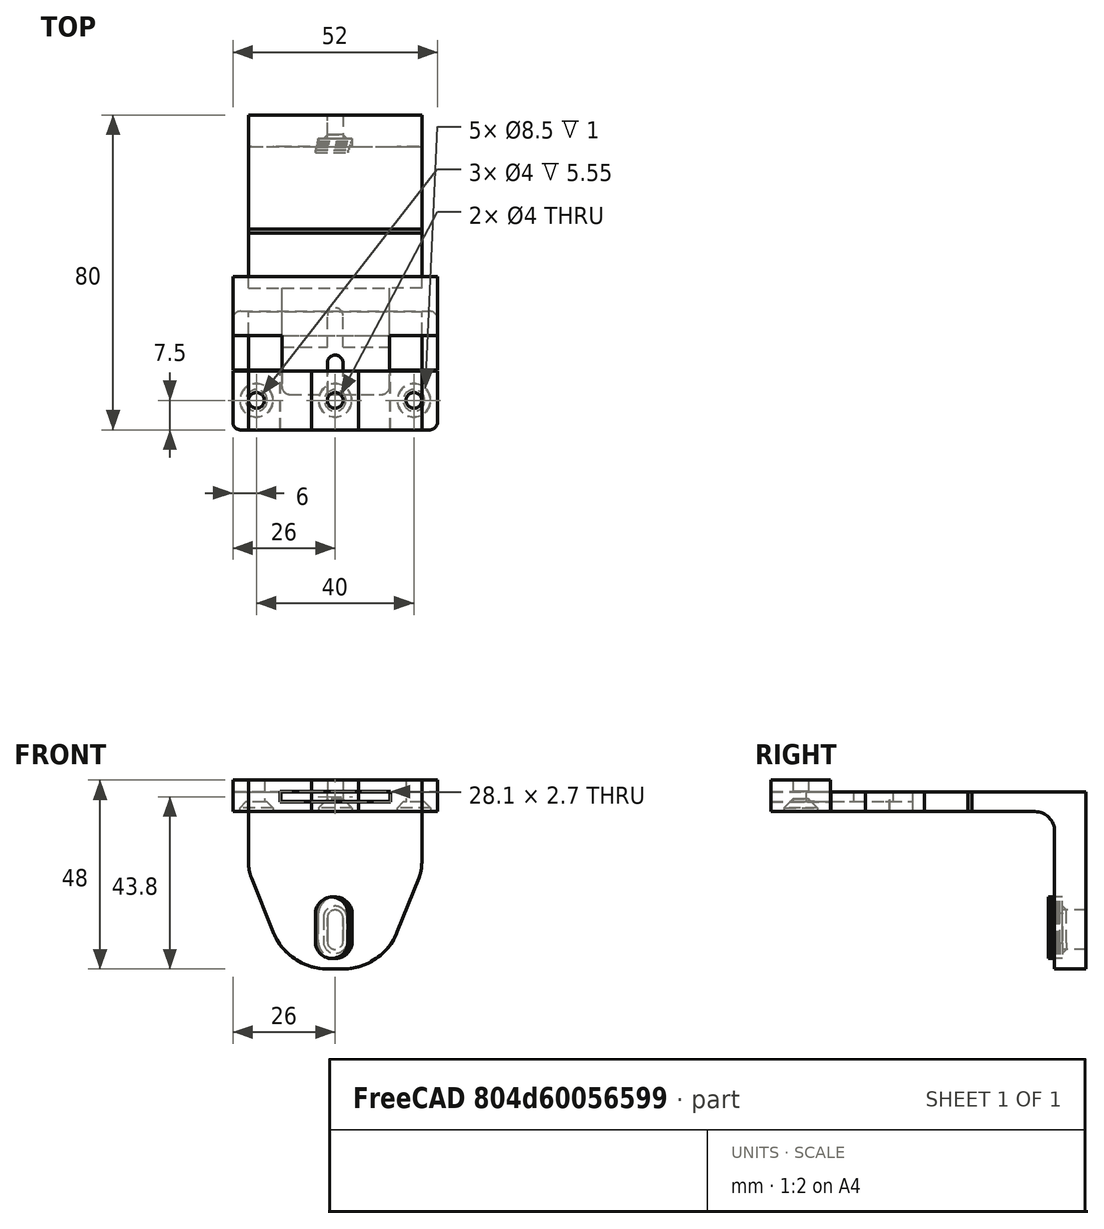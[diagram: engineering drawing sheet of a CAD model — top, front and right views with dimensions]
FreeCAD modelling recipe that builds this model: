
FCSTD DOCUMENT  (FreeCAD 0.19R24267 +99 (Git))
Label: piezas_banio_techo
License: CreativeCommons Attribution-ShareAlike
LicenseURL: http://creativecommons.org/licenses/by-sa/4.0/
objects: Part::Box×45, Part::MultiFuse×31, Part::Cut×30, Part::Cylinder×25, Part::Fillet×9, Part::Chamfer×7, Part::Feature×7, Part::FeaturePython×7, App::FeaturePython×4, App::AnnotationLabel×4, Sketcher::SketchObject×2, Part::Extrusion×2, Mesh::Feature×2, App::DocumentObjectGroup×1
note: 165 computed .brp shape members not serialized (recipe doc carries the construction recipe); baked Part::Feature solids carry a one-line shape summary decoded from their .brp

FEATURE [Part::Box] Box  label="Cube"
  AttacherType = Attacher::AttachEngine3D
  Height = 5
  Length = 44
  Width = 30
FEATURE [Part::Box] Box001  label="Cube001"
  AttacherType = Attacher::AttachEngine3D
  Height = 8
  Length = 44
  Width = 15
FEATURE [Part::MultiFuse] Fusion
  Shapes = -> [Box,Box001]
FEATURE [Part::Cylinder] Cylinder
  Angle = 360
  AttacherType = Attacher::AttachEngine3D
  Height = 10
  Placement = pos=(22,7.5,0) rot=(0,0,1;0rad)
  Radius = 2
FEATURE [Part::Cylinder] Cylinder001
  Angle = 360
  AttacherType = Attacher::AttachEngine3D
  Height = 10
  Placement = pos=(22,7.5,7) rot=(0,0,1;0rad)
  Radius = 4.25
FEATURE [Part::MultiFuse] Fusion001
  Shapes = -> [Cylinder,Cylinder001]
FEATURE [Part::Cut] Cut
  Base = -> Fusion
  Tool = -> Fusion001
FEATURE [Part::Chamfer] Chamfer  label="pieza_exterior_x_4_1"
  Base = -> Cut
  Edges = 1 edges r=2.2: [Edge31]
FEATURE [Part::Box] Box002  label="Cube002"
  AttacherType = Attacher::AttachEngine3D
  Height = 5
  Length = 44
  Placement = pos=(0,50,0) rot=(0,0,1;0rad)
  Width = 30
FEATURE [Part::Box] Box003  label="Cube003"
  AttacherType = Attacher::AttachEngine3D
  Height = 15
  Length = 44
  Placement = pos=(0,72,-15) rot=(0,0,1;0rad)
  Width = 8
FEATURE [Part::MultiFuse] Fusion002
  Shapes = -> [Box002,Box003]
FEATURE [Part::Fillet] Fillet
  Base = -> Fusion002
  Edges = 1 edges r=5: [Edge13]
FEATURE [Part::Box] Box004  label="Cube004"
  AttacherType = Attacher::AttachEngine3D
  Height = 45
  Length = 24
  Placement = pos=(10,72,-40) rot=(0,0,1;0rad)
  Width = 8
FEATURE [Part::MultiFuse] Fusion003
  Shapes = -> [Fillet,Box004]
FEATURE [Sketcher::SketchObject] Sketch
  ExternalGeometry = -> [Fusion003]
  FullyConstrained = false
  MapMode = 5
  Placement = pos=(0,80,0) rot=(0,0.707107,0.707107;3.14159rad)
  Support = -> [Fusion003]
  sketch-geometry (6):
    g0: LineSegment StartX=-44 StartY=-15 StartZ=0 EndX=-34 EndY=-40 EndZ=0
    g1: LineSegment StartX=-34 StartY=-40 StartZ=0 EndX=-34 EndY=-15 EndZ=0
    g2: LineSegment StartX=-34 StartY=-15 StartZ=0 EndX=-44 EndY=-15 EndZ=0
    g3: LineSegment StartX=-10 StartY=-15 StartZ=0 EndX=0 EndY=-15 EndZ=0
    g4: LineSegment StartX=0 StartY=-15 StartZ=0 EndX=-10 EndY=-40 EndZ=0
    g5: LineSegment StartX=-10 StartY=-40 StartZ=0 EndX=-10 EndY=-15 EndZ=0
  constraints (12):
    c: Coincident(g0,g1)
    c: Coincident(g1,g2)
    c: Coincident(g0,g2)
    c: Coincident(g0,g-3)
    c: Coincident(g1,g-3)
    c: Coincident(g0,g-4)
    c: Coincident(g3,g4)
    c: Coincident(g4,g5)
    c: Coincident(g3,g5)
    c: Coincident(g3,g-5)
    c: Coincident(g3,g-5)
    c: Coincident(g4,g-4)
FEATURE [Part::Extrusion] Extrude
  Base = -> Sketch
  Dir = (0,1,-2e-16)
  DirMode = 2
  FaceMakerClass = Part::FaceMakerBullseye
  LengthFwd = -8
  LengthRev = 0
  Solid = true
  Symmetric = false
FEATURE [Part::MultiFuse] Fusion004
  Shapes = -> [Fusion003,Extrude]
FEATURE [Part::Fillet] Fillet001
  Base = -> Fusion004
  Edges = 2 edges r=15: [Edge12,Edge14]
FEATURE [Part::Fillet] Fillet002
  Base = -> Fillet001
  Edges = 2 edges r=10: [Edge26,Edge39]
FEATURE [Part::Cylinder] Cylinder002
  Angle = 360
  AttacherType = Attacher::AttachEngine3D
  Height = 10
  Placement = pos=(22,89,-33) rot=(1,0,0;1.5708rad)
  Radius = 4.25
FEATURE [Part::Cylinder] Cylinder003
  Angle = 360
  AttacherType = Attacher::AttachEngine3D
  Height = 10
  Placement = pos=(22,80,-33) rot=(1,0,0;1.5708rad)
  Radius = 2
FEATURE [Part::MultiFuse] Fusion005
  Shapes = -> [Cylinder002,Cylinder003]
FEATURE [Part::Cut] Cut001
  Base = -> Fillet002
  Tool = -> Fusion005
FEATURE [Part::Chamfer] Chamfer001  label="pieza_interior_x4_1"
  Base = -> Cut001
  Edges = 1 edges r=2.2: [Edge50]
FEATURE [Part::Cylinder] Cylinder004
  Angle = 360
  AttacherType = Attacher::AttachEngine3D
  Height = 10
  Placement = pos=(22,80,-33) rot=(1,0,0;1.5708rad)
  Radius = 2
FEATURE [Part::Cylinder] Cylinder005
  Angle = 360
  AttacherType = Attacher::AttachEngine3D
  Height = 10
  Placement = pos=(22,89,-33) rot=(1,0,0;1.5708rad)
  Radius = 4.25
FEATURE [Part::MultiFuse] Fusion006
  Placement = pos=(0,152,-66) rot=(1,0,0;3.14159rad)
  Shapes = -> [Cylinder005,Cylinder004]
FEATURE [Part::Cylinder] Cylinder006
  Angle = 360
  AttacherType = Attacher::AttachEngine3D
  Height = 10
  Placement = pos=(22,80,-33) rot=(1,0,0;1.5708rad)
  Radius = 4.25
FEATURE [Part::MultiFuse] Fusion007
  Shapes = -> [Chamfer001,Cylinder006]
FEATURE [Part::Cut] Cut002
  Base = -> Fusion007
  Tool = -> Fusion006
FEATURE [Part::Chamfer] Chamfer002  label="pieza_interior_x4"
  Base = -> Cut002
  Edges = 1 edges r=2.2: [Edge55]
FEATURE [Part::Cylinder] Cylinder007
  Angle = 360
  AttacherType = Attacher::AttachEngine3D
  Height = 10
  Placement = pos=(22,7.5,7) rot=(0,0,1;0rad)
  Radius = 4.25
FEATURE [Part::Cylinder] Cylinder008
  Angle = 360
  AttacherType = Attacher::AttachEngine3D
  Height = 10
  Placement = pos=(22,7.5,0) rot=(0,0,1;0rad)
  Radius = 2
FEATURE [Part::MultiFuse] Fusion008
  Placement = pos=(0,15,8) rot=(1,0,0;3.14159rad)
  Shapes = -> [Cylinder008,Cylinder007]
FEATURE [Part::Cylinder] Cylinder009
  Angle = 360
  AttacherType = Attacher::AttachEngine3D
  Height = 8
  Placement = pos=(22,7.5,0) rot=(0,0,1;0rad)
  Radius = 4.25
FEATURE [Part::MultiFuse] Fusion009
  Shapes = -> [Chamfer,Cylinder009]
FEATURE [Part::Cut] Cut003
  Base = -> Fusion009
  Tool = -> Fusion008
FEATURE [Part::Chamfer] Chamfer003  label="pieza_exterior_x_4"
  Base = -> Cut003
  Edges = 1 edges r=2.2: [Edge7]
FEATURE [Part::Cylinder] Cylinder010
  Angle = 360
  AttacherType = Attacher::AttachEngine3D
  Height = 10
  Placement = pos=(22,80,-33) rot=(1,0,0;1.5708rad)
  Radius = 4.25
FEATURE [Part::Cylinder] Cylinder011
  Angle = 360
  AttacherType = Attacher::AttachEngine3D
  Height = 10
  Placement = pos=(22,80,-33) rot=(1,0,0;1.5708rad)
  Radius = 2
FEATURE [Part::Box] Box005  label="Cube005"
  AttacherType = Attacher::AttachEngine3D
  Height = 5
  Length = 44
  Placement = pos=(0,50,0) rot=(0,0,1;0rad)
  Width = 30
FEATURE [Part::Cylinder] Cylinder012
  Angle = 360
  AttacherType = Attacher::AttachEngine3D
  Height = 10
  Placement = pos=(22,89,-33) rot=(1,0,0;1.5708rad)
  Radius = 4.25
FEATURE [Part::Box] Box006  label="Cube006"
  AttacherType = Attacher::AttachEngine3D
  Height = 15
  Length = 44
  Placement = pos=(0,72,-15) rot=(0,0,1;0rad)
  Width = 8
FEATURE [Part::Box] Box007  label="Cube007"
  AttacherType = Attacher::AttachEngine3D
  Height = 45
  Length = 24
  Placement = pos=(10,72,-40) rot=(0,0,1;0rad)
  Width = 8
FEATURE [Part::Cylinder] Cylinder013
  Angle = 360
  AttacherType = Attacher::AttachEngine3D
  Height = 10
  Placement = pos=(22,80,-33) rot=(1,0,0;1.5708rad)
  Radius = 2
FEATURE [Part::Cylinder] Cylinder014
  Angle = 360
  AttacherType = Attacher::AttachEngine3D
  Height = 10
  Placement = pos=(22,89,-33) rot=(1,0,0;1.5708rad)
  Radius = 4.25
FEATURE [Part::MultiFuse] Fusion010
  Shapes = -> [Cylinder012,Cylinder011]
FEATURE [Part::MultiFuse] Fusion013
  Placement = pos=(0,152,-66) rot=(1,0,0;3.14159rad)
  Shapes = -> [Cylinder014,Cylinder013]
FEATURE [Part::MultiFuse] Fusion014
  Shapes = -> [Box005,Box006]
FEATURE [Part::Fillet] Fillet003
  Base = -> Fusion014
  Edges = 1 edges r=5: [Edge13]
FEATURE [Part::MultiFuse] Fusion012
  Shapes = -> [Fillet003,Box007]
FEATURE [Sketcher::SketchObject] Sketch001
  ExternalGeometry = -> [Fusion012]
  FullyConstrained = false
  MapMode = 5
  Placement = pos=(0,80,0) rot=(0,0.707107,0.707107;3.14159rad)
  Support = -> [Fusion012]
  sketch-geometry (6):
    g0: LineSegment StartX=-44 StartY=-15 StartZ=0 EndX=-34 EndY=-40 EndZ=0
    g1: LineSegment StartX=-34 StartY=-40 StartZ=0 EndX=-34 EndY=-15 EndZ=0
    g2: LineSegment StartX=-34 StartY=-15 StartZ=0 EndX=-44 EndY=-15 EndZ=0
    g3: LineSegment StartX=-10 StartY=-15 StartZ=0 EndX=0 EndY=-15 EndZ=0
    g4: LineSegment StartX=0 StartY=-15 StartZ=0 EndX=-10 EndY=-40 EndZ=0
    g5: LineSegment StartX=-10 StartY=-40 StartZ=0 EndX=-10 EndY=-15 EndZ=0
  constraints (12):
    c: Coincident(g0,g1)
    c: Coincident(g1,g2)
    c: Coincident(g0,g2)
    c: Coincident(g0,g-3)
    c: Coincident(g1,g-3)
    c: Coincident(g0,g-4)
    c: Coincident(g3,g4)
    c: Coincident(g4,g5)
    c: Coincident(g3,g5)
    c: Coincident(g3,g-5)
    c: Coincident(g3,g-5)
    c: Coincident(g4,g-4)
FEATURE [Part::Extrusion] Extrude001
  Base = -> Sketch001
  Dir = (0,1,-2e-16)
  DirMode = 2
  FaceMakerClass = Part::FaceMakerBullseye
  LengthFwd = -8
  LengthRev = 0
  Solid = true
  Symmetric = false
FEATURE [Part::MultiFuse] Fusion015
  Shapes = -> [Fusion012,Extrude001]
FEATURE [Part::Fillet] Fillet005
  Base = -> Fusion015
  Edges = 2 edges r=15: [Edge12,Edge14]
FEATURE [Part::Fillet] Fillet004
  Base = -> Fillet005
  Edges = 2 edges r=10: [Edge26,Edge39]
FEATURE [Part::Cut] Cut004
  Base = -> Fillet004
  Tool = -> Fusion010
FEATURE [Part::Chamfer] Chamfer004  label="pieza_interior_x4_002"
  Base = -> Cut004
  Edges = 1 edges r=2.2: [Edge50]
FEATURE [Part::MultiFuse] Fusion011
  Shapes = -> [Chamfer004,Cylinder010]
FEATURE [Part::Cut] Cut005
  Base = -> Fusion011
  Tool = -> Fusion013
FEATURE [Part::Chamfer] Chamfer005  label="pieza_interior_x005"
  Base = -> Cut005
  Edges = 1 edges r=2.2: [Edge55]
FEATURE [Part::Cylinder] Cylinder015
  Angle = 360
  AttacherType = Attacher::AttachEngine3D
  Height = 10
  Placement = pos=(22,80,-27) rot=(1,0,0;1.5708rad)
  Radius = 2
FEATURE [Part::Box] Box008  label="Cube008"
  AttacherType = Attacher::AttachEngine3D
  Height = 6
  Length = 4
  Placement = pos=(20,69,-33) rot=(0,0,1;0rad)
  Width = 16
FEATURE [Part::MultiFuse] Fusion016
  Shapes = -> [Box008,Cylinder015]
FEATURE [Part::Cylinder] Cylinder016
  Angle = 360
  AttacherType = Attacher::AttachEngine3D
  Height = 10
  Placement = pos=(22,73,-33) rot=(1,0,0;1.5708rad)
  Radius = 4.3
FEATURE [Part::Cylinder] Cylinder017
  Angle = 360
  AttacherType = Attacher::AttachEngine3D
  Height = 10
  Placement = pos=(22,73,-26) rot=(1,0,0;1.5708rad)
  Radius = 4.3
FEATURE [Part::Box] Box009  label="Cube009"
  AttacherType = Attacher::AttachEngine3D
  Height = 7.6
  Length = 8.6
  Placement = pos=(17.7,59,-33.3) rot=(0,0,1;0rad)
  Width = 14
FEATURE [Part::MultiFuse] Fusion017  label="corta_grande"
  Placement = pos=(0,1,0) rot=(0,0,1;0rad)
  Shapes = -> [Cylinder016,Box009,Cylinder017]
FEATURE [Part::Cylinder] Cylinder018
  Angle = 360
  AttacherType = Attacher::AttachEngine3D
  Height = 10
  Placement = pos=(22,80,-33) rot=(1,0,0;1.5708rad)
  Radius = 2
FEATURE [Part::Cylinder] Cylinder019
  Angle = 360
  AttacherType = Attacher::AttachEngine3D
  Height = 10
  Placement = pos=(22,89,-33) rot=(1,0,0;1.5708rad)
  Radius = 4.25
FEATURE [Part::MultiFuse] Fusion018
  Shapes = -> [Cylinder019,Cylinder018]
FEATURE [Part::MultiFuse] Fusion019  label="corta_chico"
  Placement = pos=(0,2,0) rot=(0,0,1;0rad)
  Shapes = -> [Fusion016,Fusion018]
FEATURE [Part::Box] Box010  label="Cube010"
  AttacherType = Attacher::AttachEngine3D
  Height = 10
  Length = 15
  Placement = pos=(14,72,-38) rot=(0,0,1;0rad)
  Width = 8
FEATURE [Part::MultiFuse] Fusion020
  Shapes = -> [Chamfer005,Box010]
FEATURE [Part::Cut] Cut006
  Base = -> Fusion020
  Tool = -> Fusion019
FEATURE [Part::Box] Box011  label="Cube011"
  AttacherType = Attacher::AttachEngine3D
  Height = 7.6
  Length = 8.6
  Placement = pos=(17.7,59,-33.3) rot=(0,0,1;0rad)
  Width = 14
FEATURE [Part::Cylinder] Cylinder020
  Angle = 360
  AttacherType = Attacher::AttachEngine3D
  Height = 10
  Placement = pos=(22,73,-33) rot=(1,0,0;1.5708rad)
  Radius = 4.3
FEATURE [Part::Cylinder] Cylinder021
  Angle = 360
  AttacherType = Attacher::AttachEngine3D
  Height = 10
  Placement = pos=(22,73,-26) rot=(1,0,0;1.5708rad)
  Radius = 4.3
FEATURE [Part::MultiFuse] Fusion021  label="corta_grande001"
  Placement = pos=(0,1,0) rot=(0,0,1;0rad)
  Shapes = -> [Cylinder020,Box011,Cylinder021]
FEATURE [Part::Cut] Cut007
  Base = -> Cut006
  Tool = -> Fusion017
FEATURE [Part::Feature] Cut007001  label="Cut008"
  shape: bbox 44 x 30 x 45 mm, 28 faces (baked)
FEATURE [Part::Chamfer] Chamfer006  label="pieza_exterior_x4_movil"
  Base = -> Cut007001
  Edges = 8 edges r=1: [Edge59,Edge60,Edge61,Edge62,Edge63,Edge64,Edge65,Edge66]
FEATURE [Part::Box] Box012  label="Cube012"
  AttacherType = Attacher::AttachEngine3D
  Height = 20
  Length = 20
  Placement = pos=(10,53.4,-39) rot=(0,0,1;0rad)
  Width = 20
FEATURE [Part::Cut] Cut007002  label="tapita"
  Base = -> Fusion021
  Tool = -> Box012
FEATURE [Part::Feature] Cut007002001  label="Scale_100"
  shape: bbox 8.6 x 0.6 x 15.6 mm, 10 faces (baked)
FEATURE [Part::FeaturePython] Scale  label="Scale_096"  # Draft clone (typed FeaturePython)
  Fuse = false
  Objects = -> [Cut007002001]
  Scale = (0.96,0.96,1)
FEATURE [Part::FeaturePython] Scale001  label="Scale_097"  # Draft clone (typed FeaturePython)
  Fuse = false
  Objects = -> [Cut007002001]
  Scale = (0.97,0.97,1)
FEATURE [Part::FeaturePython] Scale002  label="Scale_098"  # Draft clone (typed FeaturePython)
  Fuse = false
  Objects = -> [Cut007002001]
  Scale = (0.98,0.98,1)
FEATURE [Part::FeaturePython] Scale003  label="Scale_099"  # Draft clone (typed FeaturePython)
  Fuse = false
  Objects = -> [Cut007002001]
  Scale = (0.99,0.99,1)
FEATURE [Part::Box] Box013  label="Cube013"
  AttacherType = Attacher::AttachEngine3D
  Height = 5
  Length = 44
  Width = 30
FEATURE [Part::Box] Box014  label="Cube014"
  AttacherType = Attacher::AttachEngine3D
  Height = 2.6
  Length = 44
  Width = 15
FEATURE [Part::Cut] Cut007002002
  Base = -> Box013
  Tool = -> Box014
FEATURE [Part::Box] Box015  label="Cube015"
  AttacherType = Attacher::AttachEngine3D
  Height = 10
  Length = 8.52
  Width = 15
FEATURE [Part::Box] Box016  label="Cube016"
  AttacherType = Attacher::AttachEngine3D
  Height = 10
  Length = 8.2
  Placement = pos=(35.8,0,0) rot=(0,0,1;0rad)
  Width = 15
FEATURE [Part::Cut] Cut007002003
  Base = -> Cut007002002
  Tool = -> Box015
FEATURE [Part::Cut] Cut007002004  label="exterior_part1_1"
  Base = -> Cut007002003
  Tool = -> Box016
FEATURE [Part::Cylinder] Cylinder022
  Angle = 360
  AttacherType = Attacher::AttachEngine3D
  Height = 10
  Placement = pos=(22,8,0) rot=(0,0,1;0rad)
  Radius = 2
FEATURE [Part::Box] Box017  label="Cube017"
  AttacherType = Attacher::AttachEngine3D
  Height = 10
  Length = 4
  Placement = pos=(20,-8,0) rot=(0,0,1;0rad)
  Width = 16
FEATURE [Part::MultiFuse] Fusion022
  Shapes = -> [Cylinder022,Box017]
FEATURE [Part::Cut] Cut007002005  label="exterior_part1"
  Base = -> Cut007002004
  Placement = pos=(0,21,0) rot=(0,0,1;0rad)
  Tool = -> Fusion022
FEATURE [Part::Feature] Chamfer003001  label="pieza_exterior_x_005"
  shape: bbox 44 x 30 x 8 mm, 12 faces (baked)
FEATURE [Part::Box] Box018  label="Cube018"
  AttacherType = Attacher::AttachEngine3D
  Height = 2.5
  Length = 28
  Placement = pos=(8,0,2.55) rot=(0,0,1;0rad)
  Width = 22
FEATURE [Part::Cut] Cut007002006
  Base = -> Chamfer003001
  Tool = -> Box018
FEATURE [Part::Box] Box019  label="Cube019"
  AttacherType = Attacher::AttachEngine3D
  Height = 10
  Length = 44
  Placement = pos=(0,15,0) rot=(0,0,1;0rad)
  Width = 20
FEATURE [Part::Cut] Cut007002007  label="exterior_part21"
  Base = -> Cut007002006
  Tool = -> Box019
FEATURE [Part::Box] Box020  label="Cube020"
  AttacherType = Attacher::AttachEngine3D
  Height = 2.7
  Length = 28.1
  Placement = pos=(7.95,-2,2.45) rot=(0,0,1;0rad)
  Width = 20
FEATURE [Part::Cut] Cut007002008  label="exterior_part2"
  Base = -> Cut007002007
  Tool = -> Box020
FEATURE [Part::Box] Box021  label="Cube021"
  AttacherType = Attacher::AttachEngine3D
  Height = 2.5
  Length = 28
  Placement = pos=(8,0,2.55) rot=(0,0,1;0rad)
  Width = 22
FEATURE [Part::Box] Box022  label="Cube022"
  AttacherType = Attacher::AttachEngine3D
  Height = 10
  Length = 44
  Placement = pos=(0,15,0) rot=(0,0,1;0rad)
  Width = 20
FEATURE [Part::Box] Box023  label="Cube023"
  AttacherType = Attacher::AttachEngine3D
  Height = 2.7
  Length = 28.1
  Placement = pos=(7.95,-2,2.45) rot=(0,0,1;0rad)
  Width = 20
FEATURE [Part::Feature] Chamfer003002  label="pieza_exterior_x_006"
  shape: bbox 44 x 30 x 8 mm, 12 faces (baked)
FEATURE [Part::Cut] Cut007002009
  Base = -> Chamfer003002
  Tool = -> Box021
FEATURE [Part::Cut] Cut007002010  label="exterior_part022"
  Base = -> Cut007002009
  Tool = -> Box022
FEATURE [Part::Cut] Cut007002011  label="nuevo_exterior_atornillada"
  Base = -> Cut007002010
  Tool = -> Box023
FEATURE [Part::Box] Box024  label="Cube024"
  AttacherType = Attacher::AttachEngine3D
  Height = 8
  Length = 10
  Placement = pos=(-4,0,0) rot=(0,0,1;0rad)
  Width = 15
FEATURE [Part::Box] Box025  label="Cube025"
  AttacherType = Attacher::AttachEngine3D
  Height = 8
  Length = 10
  Placement = pos=(38,0,0) rot=(0,0,1;0rad)
  Width = 15
FEATURE [Part::MultiFuse] Fusion023  label="exterior_parte1_V2_0001"
  Refine = true
  Shapes = -> [Cut007002011,Box024,Box025]
FEATURE [Part::Box] Box026  label="Cube026"
  AttacherType = Attacher::AttachEngine3D
  Height = 5
  Length = 44
  Width = 30
FEATURE [Part::Box] Box027  label="Cube027"
  AttacherType = Attacher::AttachEngine3D
  Height = 2.6
  Length = 44
  Width = 15
FEATURE [Part::Box] Box028  label="Cube028"
  AttacherType = Attacher::AttachEngine3D
  Height = 10
  Length = 8.52
  Width = 15
FEATURE [Part::Box] Box029  label="Cube029"
  AttacherType = Attacher::AttachEngine3D
  Height = 10
  Length = 8.2
  Placement = pos=(35.8,0,0) rot=(0,0,1;0rad)
  Width = 15
FEATURE [Part::Box] Box030  label="Cube030"
  AttacherType = Attacher::AttachEngine3D
  Height = 10
  Length = 4
  Placement = pos=(20,-8,0) rot=(0,0,1;0rad)
  Width = 16
FEATURE [Part::Cut] Cut007002012
  Base = -> Box026
  Tool = -> Box027
FEATURE [Part::Cut] Cut007002013
  Base = -> Cut007002012
  Tool = -> Box028
FEATURE [Part::Cut] Cut007002014  label="exterior_part1_002"
  Base = -> Cut007002013
  Tool = -> Box029
FEATURE [Part::Cylinder] Cylinder023
  Angle = 360
  AttacherType = Attacher::AttachEngine3D
  Height = 10
  Placement = pos=(22,8,0) rot=(0,0,1;0rad)
  Radius = 2
FEATURE [Part::MultiFuse] Fusion024
  Shapes = -> [Cylinder023,Box030]
FEATURE [Part::Cut] Cut007002015  label="exterior_part023"
  Base = -> Cut007002014
  Placement = pos=(0,21,0) rot=(0,0,1;0rad)
  Tool = -> Fusion024
FEATURE [Part::Box] Box031  label="Cube031"
  AttacherType = Attacher::AttachEngine3D
  Height = 5
  Length = 10
  Placement = pos=(-4,36,0) rot=(0,0,1;0rad)
  Width = 15
FEATURE [Part::Box] Box032  label="Cube032"
  AttacherType = Attacher::AttachEngine3D
  Height = 5
  Length = 10
  Placement = pos=(38,36,0) rot=(0,0,1;0rad)
  Width = 15
FEATURE [Part::MultiFuse] Fusion025
  Refine = true
  Shapes = -> [Cut007002015,Box031,Box032]
FEATURE [Part::Box] Box033  label="Cube033"
  AttacherType = Attacher::AttachEngine3D
  Height = 2.4
  Length = 27.28
  Placement = pos=(8.5,21,2.5) rot=(0,0,1;0rad)
  Width = 15
FEATURE [Part::MultiFuse] Fusion026
  Refine = true
  Shapes = -> [Fusion025,Box033]
FEATURE [Part::Fillet] Fillet006  label="exterior_parte2_V2_base"
  Base = -> Fusion026
  Edges = 2 edges r=2: [Edge8,Edge43]
  Placement = pos=(0,-12,0.05) rot=(0,0,1;0rad)
FEATURE [Part::Feature] Fusion023001
  shape: bbox 52 x 15 x 8 mm, 14 faces (baked)
FEATURE [Part::Box] Box034  label="Cube034"
  AttacherType = Attacher::AttachEngine3D
  Height = 5.55
  Length = 15
  Placement = pos=(14,0,2.45) rot=(0,0,1;0rad)
  Width = 15
FEATURE [Part::Cylinder] Cylinder024
  Angle = 360
  AttacherType = Attacher::AttachEngine3D
  Height = 17
  Placement = pos=(22,7.5,0) rot=(0,0,1;0rad)
  Radius = 2
FEATURE [Part::Cut] Cut007002016
  Base = -> Box034
  Refine = true
  Tool = -> Cylinder024
FEATURE [Part::MultiFuse] Fusion023002
  Refine = true
  Shapes = -> [Fusion023001,Cut007002016]
FEATURE [Part::Box] Box035  label="Cube035"
  AttacherType = Attacher::AttachEngine3D
  Height = 11
  Length = 20
  Placement = pos=(-4,0,0) rot=(0,0,1;0rad)
  Width = 15
FEATURE [Part::Box] Box036  label="Cube036"
  AttacherType = Attacher::AttachEngine3D
  Height = 11
  Length = 20
  Placement = pos=(28,0,0) rot=(0,0,1;0rad)
  Width = 15
FEATURE [Part::Cut] Cut007002017
  Base = -> Fusion023002
  Refine = true
  Tool = -> Box035
FEATURE [Part::Cut] Cut007002018
  Base = -> Cut007002017
  Refine = true
  Tool = -> Box036
FEATURE [Part::Feature] Cut007002018_solid  label="Cut007002018 (Solid)"
  Placement = pos=(-20,0,0) rot=(0,0,1;0rad)
  shape: bbox 12 x 15 x 8 mm, 11 faces (baked)
FEATURE [Part::Feature] Cut007002018_solid001  label="Cut007002018 (Solid)001"
  Placement = pos=(20,0,0) rot=(0,0,1;0rad)
  shape: bbox 12 x 15 x 8 mm, 11 faces (baked)
FEATURE [Part::Box] Box037  label="Cube037"
  AttacherType = Attacher::AttachEngine3D
  Height = 8
  Length = 10
  Placement = pos=(27,0,0) rot=(0,0,1;0rad)
  Width = 15
FEATURE [Part::Box] Box038  label="Cube038"
  AttacherType = Attacher::AttachEngine3D
  Height = 8
  Length = 10
  Placement = pos=(7,0,0) rot=(0,0,1;0rad)
  Width = 15
FEATURE [Part::Cut] Cut007002019
  Base = -> Cut007002018_solid
  Refine = true
  Tool = -> Box038
FEATURE [Part::Cut] Cut007002020
  Base = -> Cut007002018_solid001
  Refine = true
  Tool = -> Box037
FEATURE [Part::Box] Box039  label="Cube039"
  AttacherType = Attacher::AttachEngine3D
  Height = 8
  Length = 11
  Placement = pos=(-4,0,0) rot=(0,0,1;0rad)
  Width = 15
FEATURE [Part::Box] Box040  label="Cube040"
  AttacherType = Attacher::AttachEngine3D
  Height = 8
  Length = 11
  Placement = pos=(37,0,0) rot=(0,0,1;0rad)
  Width = 15
FEATURE [Part::Cut] Cut007002021
  Base = -> Fusion023
  Refine = true
  Tool = -> Box039
FEATURE [Part::Cut] Cut007002022
  Base = -> Cut007002021
  Refine = true
  Tool = -> Box040
FEATURE [Part::MultiFuse] Fusion023003
  Refine = true
  Shapes = -> [Cut007002019,Cut007002020,Cut007002022]
FEATURE [Part::Box] Box041  label="Cube041"
  AttacherType = Attacher::AttachEngine3D
  Height = 2.85
  Length = 15
  Placement = pos=(15,0,5.15) rot=(0,0,1;0rad)
  Width = 15
FEATURE [Part::Box] Box042  label="Cube042"
  AttacherType = Attacher::AttachEngine3D
  Height = 2.45
  Length = 15
  Placement = pos=(15,0,0) rot=(0,0,1;0rad)
  Width = 15
FEATURE [Part::MultiFuse] Fusion023004
  Refine = true
  Shapes = -> [Fusion023003,Box041,Box042]
FEATURE [Part::Fillet] Fillet007  label="exterior_parte1_v2"
  Base = -> Fusion023004
  Edges = 2 edges r=2: [Edge1,Edge6]
FEATURE [Part::Box] Box043  label="Cube043"
  AttacherType = Attacher::AttachEngine3D
  Height = 2.4
  Length = 27.8
  Placement = pos=(8.1,2,2.6) rot=(0,0,1;0rad)
  Width = 15.15
FEATURE [Part::Box] Box044  label="Cube044"
  AttacherType = Attacher::AttachEngine3D
  Height = 5
  Length = 52
  Placement = pos=(-4,17.15,0) rot=(0,0,1;0rad)
  Width = 15
FEATURE [Part::Fillet] Fillet008
  Base = -> Box044
  Edges = 2 edges r=2: [Edge3,Edge7]
FEATURE [Part::MultiFuse] Fusion023005  label="exterior_parte2_v2"
  Placement = pos=(0,-2,0) rot=(0,0,1;0rad)
  Shapes = -> [Box043,Fillet008]
FEATURE [Mesh::Feature] Mesh  label="exterior_parte1_v2 (Meshed)"
FEATURE [Mesh::Feature] Mesh001  label="exterior_parte2_v2 (Meshed)"
FEATURE [Part::FeaturePython] Point  label="Center"  # WARN: FeaturePython — macro-defined, semantics opaque (R4)
  Placement = pos=(2,7.5,0) rot=(0,0,1;0rad)
  X = 2
  Y = 7.5
  Z = 0
FEATURE [App::FeaturePython] Dimension  label="Radius"  # Draft dimension (typed FeaturePython)
  Diameter = false
  Dimline = (4.125,7.5,0)
  Direction = (0,0,0)
  Distance = 4.25
  End = (2,7.5,0)
  Normal = (0,0,-1)
  Start = (6.25,7.5,0)
FEATURE [App::AnnotationLabel] RadiusLbl
  BasePosition = (4.125,7.5,0)
  LabelText = radi: 4.25 mm
  TextPosition = (0,0,0)
FEATURE [Part::FeaturePython] Point001  label="Center001"  # WARN: FeaturePython — macro-defined, semantics opaque (R4)
  Placement = pos=(2,7.5,0) rot=(0,0,1;0rad)
  X = 2
  Y = 7.5
  Z = 0
FEATURE [App::FeaturePython] Dimension001  label="Radius001"  # Draft dimension (typed FeaturePython)
  Diameter = false
  Dimline = (4.125,7.5,0)
  Direction = (0,0,0)
  Distance = 4.25
  End = (2,7.5,0)
  Normal = (0,0,-1)
  Start = (6.25,7.5,0)
FEATURE [App::AnnotationLabel] RadiusLbl001
  BasePosition = (4.125,7.5,0)
  LabelText = radi: 4.25 mm
  TextPosition = (0,0,0)
FEATURE [Part::FeaturePython] Point002  label="Center002"  # WARN: FeaturePython — macro-defined, semantics opaque (R4)
  Placement = pos=(2,7.5,0) rot=(0,0,1;0rad)
  X = 2
  Y = 7.5
  Z = 0
FEATURE [App::FeaturePython] Dimension002  label="Radius002"  # Draft dimension (typed FeaturePython)
  Diameter = false
  Dimline = (4.125,7.5,0)
  Direction = (0,0,0)
  Distance = 4.25
  End = (2,7.5,0)
  Normal = (0,0,-1)
  Start = (6.25,7.5,0)
FEATURE [App::AnnotationLabel] RadiusLbl002
  BasePosition = (4.125,7.5,0)
  LabelText = radi: 4.25 mm
  TextPosition = (0,0,0)
FEATURE [App::DocumentObjectGroup] Measurements
  Group = -> [Point,Dimension,RadiusLbl,Point001,Dimension001,RadiusLbl001,Point002,Dimension002,RadiusLbl002]
FEATURE [App::FeaturePython] Dimension003  label="Distance"  # Draft dimension (typed FeaturePython)
  Diameter = false
  Dimline = (-1,8,0)
  Direction = (0,0,0)
  Distance = 6.08276
  End = (-4,8.5,0)
  Normal = (0,0,-1)
  Start = (2,7.5,0)
FEATURE [App::AnnotationLabel] DistanceLbl
  BasePosition = (-1,8,0)
  LabelText = ds: 6.082762530298219 mm | dx: 6.0 | dy: 1.0 | dz: 0.0
  TextPosition = (0,0,0)
